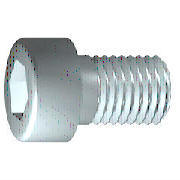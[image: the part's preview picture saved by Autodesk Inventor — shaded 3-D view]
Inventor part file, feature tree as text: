
AUTODESK INVENTOR PART (.ipt)
format: ipt  version: 2021 (Build 250183000, 183)  size: 188,416 bytes
history: native  units: mm (DEFAULTED — no unit token found)
features: sketch x2, extrude x1, plane x1, fillet x1
ambient origin geometry x7: Origin, YZ Plane, XY Plane, X Axis, Y Axis, Z Axis, Center Point
bodies: Solid1 (feature_tree), Body (feature_tree)
feature tree (5):
  extrude  "Slot"  Depth=6.0mm
  plane  "Work Plane1"
  fillet  "Fillet2"  Radius=6.0mm
  sketch  "Sketch1"  dims[d1=18.0mm d2=0.61355mm d3=6.0mm]
  sketch  "Sketch2"  dims[d4=3.0mm d5=60.0deg d6=6.0mm d7=6.0mm d8=5.773503mm d9=10.0mm d10=90.0deg d11=10.0mm d12=0.0mm d13=18.0mm d14=0.0mm d15=0.61345mm d16=0.61345mm d17=0.6mm d19=0.0mm d26=40.0mm d27=45.0deg d28=0.0mm d29=0.0mm d30=0.1mm]
